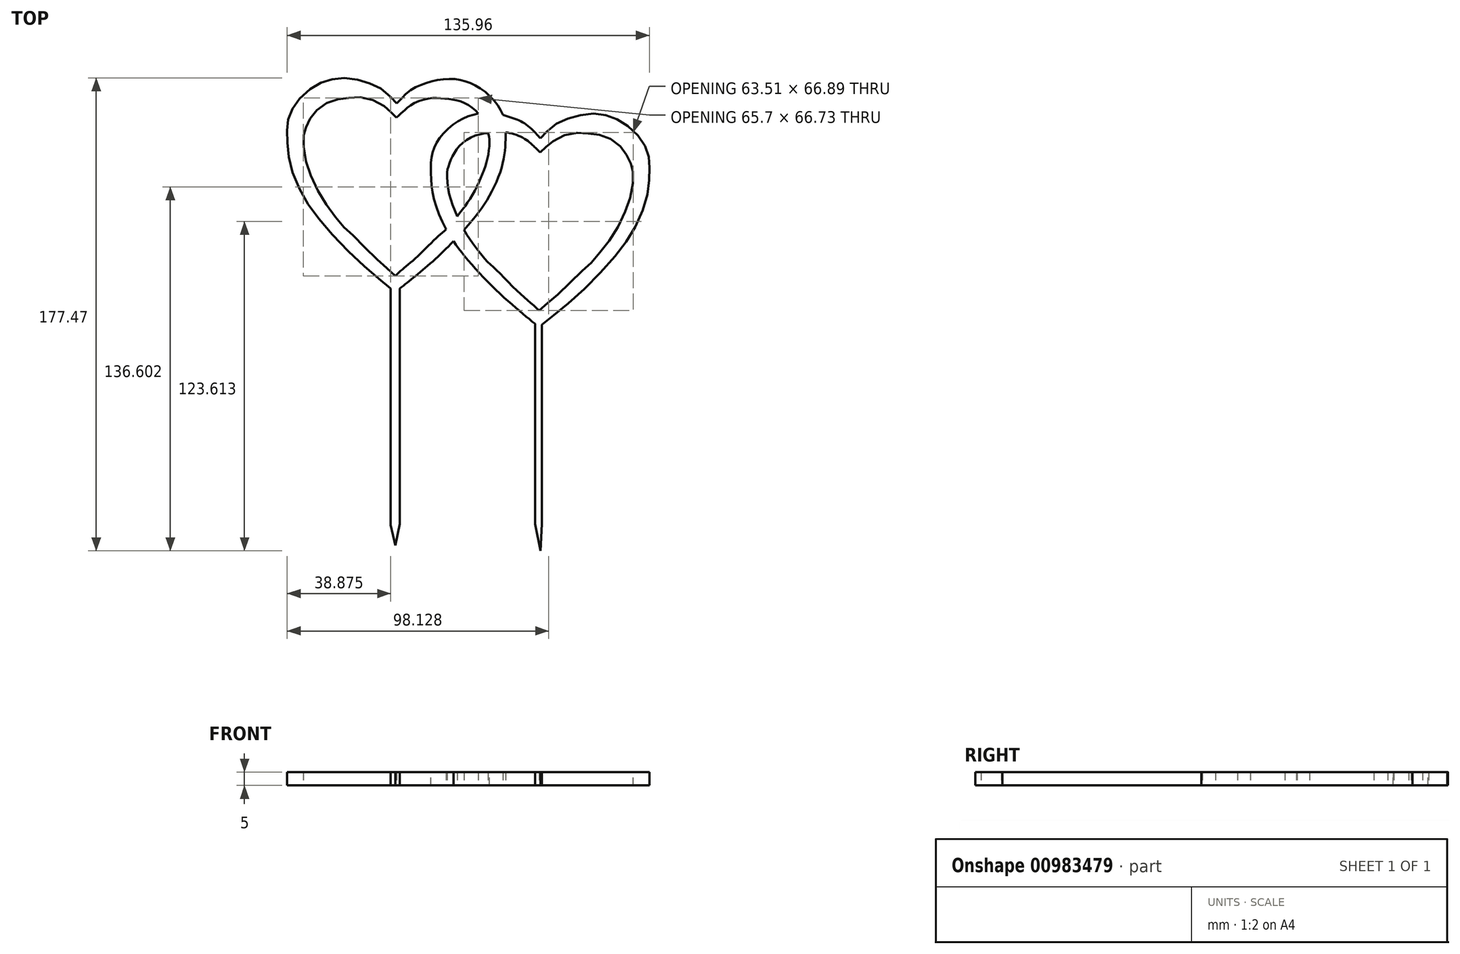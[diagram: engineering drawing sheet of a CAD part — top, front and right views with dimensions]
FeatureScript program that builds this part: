
annotation { "Feature Type Name" : "Feature", "Feature Type Description" : "" }
export const myFeature = defineFeature(function(context is Context, id is Id, definition is map)
    precondition{}
    {
        {
            var Q0;
            Q0=qCreatedBy(makeId("Top.planeOp"),FACE);
            var sketch = newSketch(context, id + "F0", { "sketchPlane" : qUnion([Q0])});
            skLineSegment(sketch, "E0", {"start": v(4.35, 24.32) * mm, "end": v(3.8, -46.47) * mm});
            skFitSpline(sketch, "E1", {"points": [v(3.8, -46.47) * mm, v(10.05, -41.54) * mm, v(20.97, -32.07) * mm, v(32.6, -19.7) * mm, v(38.96, -10.73) * mm, v(43.45, -0.75) * mm, v(45.04, 7.2) * mm, v(45.25, 12.86) * mm, v(45.08, 16.97) * mm, v(43.66, 21.29) * mm, v(40.55, 25.81) * mm, v(35.58, 30.1) * mm, v(31.02, 32.34) * mm, v(26.4, 33.45) * mm, v(20.48, 33.24) * mm, v(14.85, 31.76) * mm, v(9.95, 29.54) * mm, v(5.9, 25.95) * mm, v(4.35, 24.32) * mm], "startDerivative": vector(97.87, 76.03) * mm, "endDerivative": vector(-42.68, -45.17) * mm});
            skFitSpline(sketch, "E2.MirrorCS", {"points": [v(3.8, -46.47) * mm, v(-2.4, -41.44) * mm, v(-13.16, -31.8) * mm, v(-24.6, -19.26) * mm, v(-30.81, -10.18) * mm, v(-35.14, -0.13) * mm, v(-36.6, 7.84) * mm, v(-36.72, 13.5) * mm, v(-36.49, 17.62) * mm, v(-35, 21.91) * mm, v(-31.82, 26.39) * mm, v(-26.78, 30.59) * mm, v(-22.19, 32.76) * mm, v(-17.54, 33.8) * mm, v(-11.64, 33.5) * mm, v(-6.04, 31.92) * mm, v(-1.17, 29.63) * mm, v(2.82, 25.98) * mm, v(4.35, 24.32) * mm], "startDerivative": vector(-96.66, 77.57) * mm, "endDerivative": vector(41.96, -45.83) * mm});
            skFitSpline(sketch, "E3", {"points": [v(3.84, -40.36) * mm, v(7.1, -37.42) * mm, v(12.17, -33.08) * mm, v(19.48, -25.94) * mm, v(23.43, -22.4) * mm, v(27.5, -17.56) * mm, v(32.42, -10.61) * mm, v(36.53, -2.2) * mm, v(38.66, 4.75) * mm, v(39.16, 11.07) * mm, v(38.79, 12.92) * mm, v(37.88, 15.8) * mm, v(36.32, 18.71) * mm, v(33.78, 21.83) * mm, v(29.38, 24.7) * mm, v(25.15, 25.82) * mm, v(20.88, 26.27) * mm, v(16.32, 26.19) * mm, v(10.45, 24.13) * mm, v(7.32, 21.8) * mm, v(5.95, 20.55) * mm, v(4.3, 19.06) * mm], "startDerivative": vector(69.42, 64.82) * mm, "endDerivative": vector(-53.92, -48.67) * mm});
            skFitSpline(sketch, "E4.MirrorCS", {"points": [v(3.84, -40.36) * mm, v(0.63, -37.37) * mm, v(-4.38, -32.95) * mm, v(-11.57, -25.69) * mm, v(-15.46, -22.1) * mm, v(-19.45, -17.19) * mm, v(-24.27, -10.17) * mm, v(-28.24, -1.68) * mm, v(-30.27, 5.3) * mm, v(-30.66, 11.62) * mm, v(-30.26, 13.47) * mm, v(-29.31, 16.33) * mm, v(-27.7, 19.22) * mm, v(-25.11, 22.3) * mm, v(-20.67, 25.1) * mm, v(-16.42, 26.15) * mm, v(-12.15, 26.53) * mm, v(-7.59, 26.38) * mm, v(-1.75, 24.23) * mm, v(1.34, 21.84) * mm, v(2.69, 20.57) * mm, v(4.3, 19.06) * mm], "startDerivative": vector(-68.4, 65.91) * mm, "endDerivative": vector(53.15, -49.52) * mm});
            skFitSpline(sketch, "E5", {"points": [v(57.76, -59.54) * mm, v(64.02, -54.6) * mm, v(74.94, -45.14) * mm, v(86.57, -32.78) * mm, v(92.93, -23.8) * mm, v(97.42, -13.82) * mm, v(99, -5.87) * mm, v(99.22, -0.2) * mm, v(99.04, 3.9) * mm, v(97.63, 8.22) * mm, v(94.52, 12.75) * mm, v(89.55, 17.03) * mm, v(84.99, 19.27) * mm, v(80.36, 20.38) * mm, v(74.45, 20.17) * mm, v(68.82, 18.69) * mm, v(63.92, 16.48) * mm, v(59.88, 12.88) * mm, v(58.32, 11.25) * mm], "startDerivative": vector(97.87, 76.03) * mm, "endDerivative": vector(-42.68, -45.17) * mm});
            skFitSpline(sketch, "E6.MirrorCS", {"points": [v(57.76, -59.54) * mm, v(51.58, -54.5) * mm, v(40.81, -44.87) * mm, v(29.37, -32.33) * mm, v(23.16, -23.25) * mm, v(18.82, -13.2) * mm, v(17.36, -5.23) * mm, v(17.24, 0.44) * mm, v(17.48, 4.55) * mm, v(18.96, 8.84) * mm, v(22.14, 13.32) * mm, v(27.19, 17.52) * mm, v(31.78, 19.7) * mm, v(36.42, 20.72) * mm, v(42.33, 20.42) * mm, v(47.93, 18.85) * mm, v(52.8, 16.56) * mm, v(56.79, 12.9) * mm, v(58.32, 11.25) * mm], "startDerivative": vector(-96.66, 77.57) * mm, "endDerivative": vector(41.96, -45.83) * mm});
            skFitSpline(sketch, "E7", {"points": [v(57.8, -53.43) * mm, v(61.07, -50.49) * mm, v(66.14, -46.15) * mm, v(73.45, -39) * mm, v(77.4, -35.47) * mm, v(81.46, -30.63) * mm, v(86.39, -23.68) * mm, v(90.5, -15.26) * mm, v(92.63, -8.32) * mm, v(93.13, -2) * mm, v(92.76, -0.15) * mm, v(91.85, 2.73) * mm, v(90.3, 5.64) * mm, v(87.74, 8.77) * mm, v(83.35, 11.64) * mm, v(79.12, 12.75) * mm, v(74.85, 13.2) * mm, v(70.29, 13.12) * mm, v(64.41, 11.07) * mm, v(61.3, 8.72) * mm, v(59.92, 7.48) * mm, v(58.28, 5.99) * mm], "startDerivative": vector(69.42, 64.82) * mm, "endDerivative": vector(-53.92, -48.67) * mm});
            skFitSpline(sketch, "E8.MirrorCS", {"points": [v(57.8, -53.43) * mm, v(54.6, -50.44) * mm, v(49.6, -46.02) * mm, v(42.4, -38.76) * mm, v(38.5, -35.17) * mm, v(34.52, -30.25) * mm, v(29.7, -23.24) * mm, v(25.72, -14.75) * mm, v(23.7, -7.78) * mm, v(23.3, -1.45) * mm, v(23.7, 0.4) * mm, v(24.65, 3.26) * mm, v(26.26, 6.15) * mm, v(28.86, 9.23) * mm, v(33.3, 12.04) * mm, v(37.54, 13.08) * mm, v(41.82, 13.46) * mm, v(46.38, 13.3) * mm, v(52.22, 11.16) * mm, v(55.3, 8.77) * mm, v(56.65, 7.5) * mm, v(58.28, 5.99) * mm], "startDerivative": vector(-68.4, 65.91) * mm, "endDerivative": vector(53.15, -49.52) * mm});
            skLineSegment(sketch, "E9", {"start": v(0, -71.75) * mm, "end": v(78.7, -71.75) * mm});
            skLineSegment(sketch, "E10", {"start": v(56.3, -58.37) * mm, "end": v(56.3, -71.75) * mm});
            skLineSegment(sketch, "E11", {"start": v(56.3, -71.75) * mm, "end": v(58.8, -71.75) * mm});
            skLineSegment(sketch, "E12", {"start": v(58.8, -71.75) * mm, "end": v(58.8, -58.73) * mm});
            skLineSegment(sketch, "E13", {"start": v(2.13, -45.14) * mm, "end": v(5.47, -45.17) * mm});
            skLineSegment(sketch, "E14", {"start": v(5.47, -45.17) * mm, "end": v(5.47, -71.75) * mm});
            skLineSegment(sketch, "E15", {"start": v(2.13, -45.14) * mm, "end": v(2.13, -71.75) * mm});
            skLineSegment(sketch, "E16", {"start": v(2.13, -71.75) * mm, "end": v(2.13, -133.87) * mm});
            skLineSegment(sketch, "E17", {"start": v(5.47, -71.75) * mm, "end": v(5.47, -133.45) * mm});
            skLineSegment(sketch, "E18", {"start": v(5.47, -133.45) * mm, "end": v(3.88, -141.47) * mm});
            skLineSegment(sketch, "E19", {"start": v(3.88, -141.47) * mm, "end": v(2.13, -133.87) * mm});
            skLineSegment(sketch, "E20", {"start": v(56.3, -71.75) * mm, "end": v(56.3, -133.45) * mm});
            skLineSegment(sketch, "E21", {"start": v(56.3, -133.45) * mm, "end": v(58.3, -143.6) * mm});
            skLineSegment(sketch, "E22", {"start": v(58.8, -71.75) * mm, "end": v(58.8, -133.45) * mm});
            skLineSegment(sketch, "E23", {"start": v(58.8, -133.45) * mm, "end": v(58.3, -143.6) * mm});
            skSolve(sketch);
        }
        {
            var Q0;
            {var subQ1=sQuery(id+"F0.wireOp",EDGE,"E16");Q0=makeQuery(id+"F0.imprint","IMPRINT",FACE,{"disambiguationData":[TD([[makeQuery(id+"F0.imprint","IMPRINT",EDGE,{"derivedFrom":subQ1}),1.0]])]});}
            var Q1;
            {var subQ1=sQuery(id+"F0.wireOp",EDGE,"E20");Q1=makeQuery(id+"F0.imprint","IMPRINT",FACE,{"disambiguationData":[TD([[makeQuery(id+"F0.imprint","IMPRINT",EDGE,{"derivedFrom":subQ1}),1.0]])]});}
            var Q2;
            {var subQ0=sQuery(id+"F0.wireOp",EDGE,"E10");Q2=makeQuery(id+"F0.imprint","IMPRINT",FACE,{"disambiguationData":[TD([[makeQuery(id+"F0.imprint","IMPRINT",EDGE,{"derivedFrom":subQ0}),1.0]])]});}
            var Q3;
            {var subQ0=sQuery(id+"F0.wireOp",EDGE,"E14");Q3=makeQuery(id+"F0.imprint","IMPRINT",FACE,{"disambiguationData":[TD([[makeQuery(id+"F0.imprint","IMPRINT",EDGE,{"derivedFrom":subQ0}),-1.0]])]});}
            var Q4;
            {var subQ12=sQuery(id+"F0.wireOp",EDGE,"E7");Q4=makeQuery(id+"F0.imprint","IMPRINT",FACE,{"disambiguationData":[TD([[makeQuery(id+"F0.imprint","IMPRINT",EDGE,{"derivedFrom":subQ12}),-1.0]])]});}
            var Q5;
            {var subQ1=sQuery(id+"F0.wireOp",EDGE,"E1");var subQ3=sQuery(id+"F0.wireOp",EDGE,"E6.MirrorCS");var subQ4=makeQuery(id+"F0.imprint","INTERSECT",VERTEX,{"disambiguationData":[OD(1.0)],"derivedFrom":[subQ1,subQ3]});Q5=makeQuery(id+"F0.imprint","IMPRINT",FACE,{"disambiguationData":[TD([[makeQuery(id+"F0.imprint","IMPRINT",EDGE,{"disambiguationData":[TD([[subQ4,-1.0]])],"derivedFrom":subQ3}),1.0]])]});}
            var Q6;
            {var subQ0=sQuery(id+"F0.wireOp",EDGE,"E4.MirrorCS");Q6=makeQuery(id+"F0.imprint","IMPRINT",FACE,{"disambiguationData":[TD([[makeQuery(id+"F0.imprint","IMPRINT",EDGE,{"derivedFrom":subQ0}),1.0]])]});}
            var Q7;
            {var subQ1=sQuery(id+"F0.wireOp",EDGE,"E0");var subQ3=sQuery(id+"F0.wireOp",EDGE,"E13");var subQ4=makeQuery(id+"F0.imprint","INTERSECT",VERTEX,{"derivedFrom":[subQ1,subQ3]});Q7=makeQuery(id+"F0.imprint","IMPRINT",FACE,{"disambiguationData":[TD([[makeQuery(id+"F0.imprint","IMPRINT",EDGE,{"disambiguationData":[TD([[subQ4,-1.0]])],"derivedFrom":subQ1}),-1.0]])]});}
            var Q8;
            {var subQ1=sQuery(id+"F0.wireOp",EDGE,"E0");var subQ3=sQuery(id+"F0.wireOp",EDGE,"E13");var subQ4=makeQuery(id+"F0.imprint","INTERSECT",VERTEX,{"derivedFrom":[subQ1,subQ3]});Q8=makeQuery(id+"F0.imprint","IMPRINT",FACE,{"disambiguationData":[TD([[makeQuery(id+"F0.imprint","IMPRINT",EDGE,{"disambiguationData":[TD([[subQ4,-1.0]])],"derivedFrom":subQ1}),1.0]])]});}
            var Q9;
            {var subQ0=sQuery(id+"F0.wireOp",EDGE,"E6.MirrorCS");var subQ1=sQuery(id+"F0.wireOp",EDGE,"E1");var subQ2=makeQuery(id+"F0.imprint","INTERSECT",VERTEX,{"disambiguationData":[OD(1.0)],"derivedFrom":[subQ1,subQ0]});Q9=makeQuery(id+"F0.imprint","IMPRINT",FACE,{"disambiguationData":[TD([[makeQuery(id+"F0.imprint","IMPRINT",EDGE,{"disambiguationData":[TD([[subQ2,-1.0]])],"derivedFrom":subQ1}),1.0]])]});}
            var Q10;
            {var subQ0=sQuery(id+"F0.wireOp",EDGE,"E8.MirrorCS");var subQ1=sQuery(id+"F0.wireOp",EDGE,"E1");var subQ2=makeQuery(id+"F0.imprint","INTERSECT",VERTEX,{"disambiguationData":[OD(0.0)],"derivedFrom":[subQ1,subQ0]});Q10=makeQuery(id+"F0.imprint","IMPRINT",FACE,{"disambiguationData":[TD([[makeQuery(id+"F0.imprint","IMPRINT",EDGE,{"disambiguationData":[TD([[subQ2,-1.0]])],"derivedFrom":subQ1}),1.0]])]});}
            var Q11;
            {var subQ0=sQuery(id+"F0.wireOp",EDGE,"E6.MirrorCS");var subQ1=sQuery(id+"F0.wireOp",EDGE,"E3");var subQ2=makeQuery(id+"F0.imprint","INTERSECT",VERTEX,{"disambiguationData":[OD(0.0)],"derivedFrom":[subQ1,subQ0]});Q11=makeQuery(id+"F0.imprint","IMPRINT",FACE,{"disambiguationData":[TD([[makeQuery(id+"F0.imprint","IMPRINT",EDGE,{"disambiguationData":[TD([[subQ2,-1.0]])],"derivedFrom":subQ1}),1.0]])]});}
            var Q12;
            {var subQ3=sQuery(id+"F0.wireOp",EDGE,"E1");var subQ5=sQuery(id+"F0.wireOp",EDGE,"E6.MirrorCS");var subQ7=makeQuery(id+"F0.imprint","INTERSECT",VERTEX,{"disambiguationData":[OD(0.0)],"derivedFrom":[subQ3,subQ5]});Q12=makeQuery(id+"F0.imprint","IMPRINT",FACE,{"disambiguationData":[TD([[makeQuery(id+"F0.imprint","IMPRINT",EDGE,{"disambiguationData":[TD([[subQ7,1.0]])],"derivedFrom":subQ5}),1.0]])]});}
            var Q13;
            {var subQ0=sQuery(id+"F0.wireOp",EDGE,"E6.MirrorCS");var subQ1=sQuery(id+"F0.wireOp",EDGE,"E1");var subQ2=makeQuery(id+"F0.imprint","INTERSECT",VERTEX,{"disambiguationData":[OD(0.0)],"derivedFrom":[subQ1,subQ0]});Q13=makeQuery(id+"F0.imprint","IMPRINT",FACE,{"disambiguationData":[TD([[makeQuery(id+"F0.imprint","IMPRINT",EDGE,{"disambiguationData":[TD([[subQ2,1.0]])],"derivedFrom":subQ1}),1.0]])]});}
            extrude(context, id + "F1", {"entities" : qUnion([Q0, Q1, Q2, Q3, Q4, Q5, Q6, Q7, Q8, Q9, Q10, Q11, Q12, Q13]), "depth" : 5 * mm, "offsetDistance" : 25 * mm});
        }
    });
